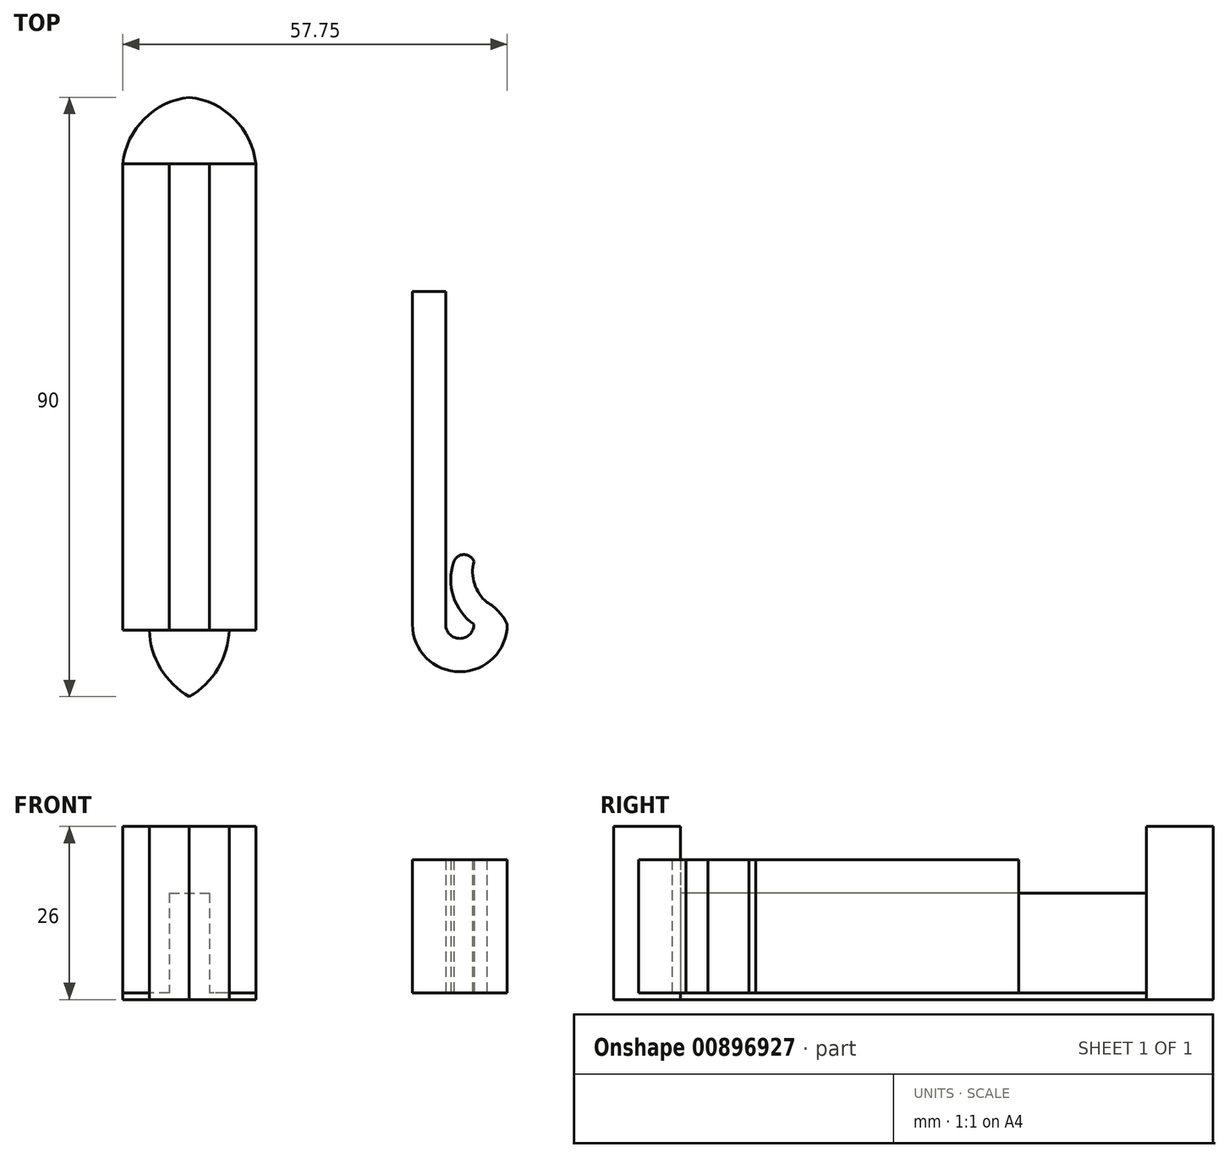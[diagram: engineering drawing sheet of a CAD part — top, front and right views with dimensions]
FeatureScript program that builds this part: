
annotation { "Feature Type Name" : "Feature", "Feature Type Description" : "" }
export const myFeature = defineFeature(function(context is Context, id is Id, definition is map)
    precondition{}
    {
        {
            var Q0;
            Q0=qCreatedBy(makeId("Top.planeOp"),FACE);
            var sketch = newSketch(context, id + "F0", { "sketchPlane" : qUnion([Q0])});
            skLineSegment(sketch, "E0", {"start": v(0, 35) * mm, "end": v(0, -35) * mm});
            skLineSegment(sketch, "E1", {"start": v(0, 35) * mm, "end": v(0, 45) * mm});
            skLineSegment(sketch, "E2", {"start": v(0, -35) * mm, "end": v(0, -45) * mm});
            skLineSegment(sketch, "E3", {"start": v(0, 35) * mm, "end": v(-10, 35) * mm});
            skLineSegment(sketch, "E4", {"start": v(0, -35) * mm, "end": v(-6, -35) * mm});
            skArc(sketch, "E5", {"start": v(0, 45) * mm, "mid": v(-6.76, 41.76) * mm, "end": v(-10, 35) * mm});
            skArc(sketch, "E6", {"start": v(-6, -35) * mm, "mid": v(-4.3, -40.78) * mm, "end": v(0, -45) * mm});
            skLineSegment(sketch, "E7", {"start": v(-3, 35) * mm, "end": v(-3, -35) * mm});
            skLineSegment(sketch, "E8", {"start": v(0, 5.3) * mm, "end": v(-3, 5.3) * mm});
            skArc(sketch, "E9.MirrorCS", {"start": v(0, 45) * mm, "mid": v(6.76, 41.76) * mm, "end": v(10, 35) * mm});
            skLineSegment(sketch, "E10.MirrorCS", {"start": v(0, 35) * mm, "end": v(10, 35) * mm});
            skLineSegment(sketch, "E11.MirrorCS", {"start": v(3, 35) * mm, "end": v(3, -35) * mm});
            skArc(sketch, "E12.MirrorCS", {"start": v(6, -35) * mm, "mid": v(4.3, -40.78) * mm, "end": v(0, -45) * mm});
            skLineSegment(sketch, "E13.MirrorCS", {"start": v(0, -35) * mm, "end": v(6, -35) * mm});
            skLineSegment(sketch, "E14", {"start": v(-10, 35) * mm, "end": v(-10, -35) * mm});
            skLineSegment(sketch, "E15", {"start": v(-10, -35) * mm, "end": v(-6, -35) * mm});
            skLineSegment(sketch, "E16.MirrorCS", {"start": v(10, -35) * mm, "end": v(6, -35) * mm});
            skLineSegment(sketch, "E17.MirrorCS", {"start": v(10, 35) * mm, "end": v(10, -35) * mm});
            skSolve(sketch);
        }
        {
            var Q0;
            {var subQ0=sQuery(id+"F0.wireOp",EDGE,"E1");Q0=makeQuery(id+"F0.imprint","IMPRINT",FACE,{"disambiguationData":[TD([[makeQuery(id+"F0.imprint","IMPRINT",EDGE,{"derivedFrom":subQ0}),1.0]])]});}
            var Q1;
            {var subQ0=sQuery(id+"F0.wireOp",EDGE,"E1");Q1=makeQuery(id+"F0.imprint","IMPRINT",FACE,{"disambiguationData":[TD([[makeQuery(id+"F0.imprint","IMPRINT",EDGE,{"derivedFrom":subQ0}),-1.0]])]});}
            var Q2;
            {var subQ3=sQuery(id+"F0.wireOp",EDGE,"E8");Q2=makeQuery(id+"F0.imprint","IMPRINT",FACE,{"disambiguationData":[TD([[makeQuery(id+"F0.imprint","IMPRINT",EDGE,{"derivedFrom":subQ3}),-1.0]])]});}
            var Q3;
            {var subQ3=sQuery(id+"F0.wireOp",EDGE,"E8");Q3=makeQuery(id+"F0.imprint","IMPRINT",FACE,{"disambiguationData":[TD([[makeQuery(id+"F0.imprint","IMPRINT",EDGE,{"derivedFrom":subQ3}),1.0]])]});}
            var Q4;
            {var subQ0=sQuery(id+"F0.wireOp",EDGE,"E2");Q4=makeQuery(id+"F0.imprint","IMPRINT",FACE,{"disambiguationData":[TD([[makeQuery(id+"F0.imprint","IMPRINT",EDGE,{"derivedFrom":subQ0}),1.0]])]});}
            var Q5;
            {var subQ2=sQuery(id+"F0.wireOp",EDGE,"E11.MirrorCS");Q5=makeQuery(id+"F0.imprint","IMPRINT",FACE,{"disambiguationData":[TD([[makeQuery(id+"F0.imprint","IMPRINT",EDGE,{"derivedFrom":subQ2}),1.0]])]});}
            var Q6;
            {var subQ3=sQuery(id+"F0.wireOp",EDGE,"E11.MirrorCS");Q6=makeQuery(id+"F0.imprint","IMPRINT",FACE,{"disambiguationData":[TD([[makeQuery(id+"F0.imprint","IMPRINT",EDGE,{"derivedFrom":subQ3}),-1.0]])]});}
            var Q7;
            {var subQ7=sQuery(id+"F0.wireOp",EDGE,"E14");Q7=makeQuery(id+"F0.imprint","IMPRINT",FACE,{"disambiguationData":[TD([[makeQuery(id+"F0.imprint","IMPRINT",EDGE,{"derivedFrom":subQ7}),1.0]])]});}
            var Q8;
            {var subQ0=sQuery(id+"F0.wireOp",EDGE,"E2");Q8=makeQuery(id+"F0.imprint","IMPRINT",FACE,{"disambiguationData":[TD([[makeQuery(id+"F0.imprint","IMPRINT",EDGE,{"derivedFrom":subQ0}),-1.0]])]});}
            extrude(context, id + "F1", {"entities" : qUnion([Q0, Q1, Q2, Q3, Q4, Q5, Q6, Q7, Q8]), "oppositeDirection" : true, "depth" : 1 * mm, "offsetDistance" : 25 * mm});
        }
        {
            var Q0;
            {var subQ3=sQuery(id+"F0.wireOp",EDGE,"E8");Q0=makeQuery(id+"F0.imprint","IMPRINT",FACE,{"disambiguationData":[TD([[makeQuery(id+"F0.imprint","IMPRINT",EDGE,{"derivedFrom":subQ3}),1.0]])]});}
            var Q1;
            {var subQ3=sQuery(id+"F0.wireOp",EDGE,"E11.MirrorCS");Q1=makeQuery(id+"F0.imprint","IMPRINT",FACE,{"disambiguationData":[TD([[makeQuery(id+"F0.imprint","IMPRINT",EDGE,{"derivedFrom":subQ3}),-1.0]])]});}
            var Q2;
            {var subQ3=sQuery(id+"F0.wireOp",EDGE,"E8");Q2=makeQuery(id+"F0.imprint","IMPRINT",FACE,{"disambiguationData":[TD([[makeQuery(id+"F0.imprint","IMPRINT",EDGE,{"derivedFrom":subQ3}),-1.0]])]});}
            extrude(context, id + "F2", {"entities" : qUnion([Q0, Q1, Q2]), "operationType" : NewBodyOperationType.ADD, "depth" : 15 * mm, "offsetDistance" : 25 * mm});
        }
        {
            var Q0;
            {var subQ0=sQuery(id+"F0.wireOp",EDGE,"E1");Q0=makeQuery(id+"F0.imprint","IMPRINT",FACE,{"disambiguationData":[TD([[makeQuery(id+"F0.imprint","IMPRINT",EDGE,{"derivedFrom":subQ0}),1.0]])]});}
            var Q1;
            {var subQ0=sQuery(id+"F0.wireOp",EDGE,"E1");Q1=makeQuery(id+"F0.imprint","IMPRINT",FACE,{"disambiguationData":[TD([[makeQuery(id+"F0.imprint","IMPRINT",EDGE,{"derivedFrom":subQ0}),-1.0]])]});}
            var Q2;
            {var subQ0=sQuery(id+"F0.wireOp",EDGE,"E2");Q2=makeQuery(id+"F0.imprint","IMPRINT",FACE,{"disambiguationData":[TD([[makeQuery(id+"F0.imprint","IMPRINT",EDGE,{"derivedFrom":subQ0}),-1.0]])]});}
            var Q3;
            {var subQ0=sQuery(id+"F0.wireOp",EDGE,"E2");Q3=makeQuery(id+"F0.imprint","IMPRINT",FACE,{"disambiguationData":[TD([[makeQuery(id+"F0.imprint","IMPRINT",EDGE,{"derivedFrom":subQ0}),1.0]])]});}
            extrude(context, id + "F3", {"entities" : qUnion([Q0, Q1, Q2, Q3]), "operationType" : NewBodyOperationType.ADD, "depth" : 25 * mm, "offsetDistance" : 25 * mm});
        }
        {
            var Q0;
            Q0=qCreatedBy(makeId("Top.planeOp"),FACE);
            var sketch = newSketch(context, id + "F4", { "sketchPlane" : qUnion([Q0])});
            skLineSegment(sketch, "E18.bottom", {"start": v(33.51, 15.84) * mm, "end": v(38.51, 15.84) * mm});
            skLineSegment(sketch, "E18.top", {"start": v(33.51, -34.16) * mm, "end": v(38.51, -34.16) * mm});
            skLineSegment(sketch, "E18.left", {"start": v(33.51, 15.84) * mm, "end": v(33.51, -34.16) * mm});
            skLineSegment(sketch, "E18.right", {"start": v(38.51, 15.84) * mm, "end": v(38.51, -34.16) * mm});
            skArc(sketch, "E19", {"start": v(33.51, -34.16) * mm, "mid": v(40.63, -41.28) * mm, "end": v(47.75, -34.16) * mm});
            skArc(sketch, "E20.0", {"start": v(38.51, -34.16) * mm, "mid": v(40.63, -36.28) * mm, "end": v(42.75, -34.16) * mm});
            skArc(sketch, "E21", {"start": v(39.75, -24.72) * mm, "mid": v(39.67, -29.94) * mm, "end": v(42.75, -34.16) * mm});
            skArc(sketch, "E22", {"start": v(47.75, -34.16) * mm, "mid": v(46.5, -32.25) * mm, "end": v(44.7, -30.83) * mm});
            skArc(sketch, "E23", {"start": v(42.75, -24.72) * mm, "mid": v(42.82, -28.06) * mm, "end": v(44.7, -30.83) * mm});
            skArc(sketch, "E24", {"start": v(42.75, -24.72) * mm, "mid": v(41.25, -23.68) * mm, "end": v(39.75, -24.72) * mm});
            skSolve(sketch);
        }
        {
            var Q0;
            Q0=makeQuery(id+"F4.imprint","IMPRINT",FACE,{"disambiguationData":[TD([[makeQuery(id+"F4.imprint","IMPRINT",EDGE,{"derivedFrom":sQuery(id+"F4.wireOp",EDGE,"E18.top")}),-1.0]])]});
            var Q1;
            Q1=makeQuery(id+"F4.imprint","IMPRINT",FACE,{"disambiguationData":[TD([[makeQuery(id+"F4.imprint","IMPRINT",EDGE,{"derivedFrom":sQuery(id+"F4.wireOp",EDGE,"E18.bottom")}),-1.0]])]});
            extrude(context, id + "F5", {"entities" : qUnion([Q0, Q1]), "depth" : 20 * mm, "offsetDistance" : 25 * mm});
        }
    });
